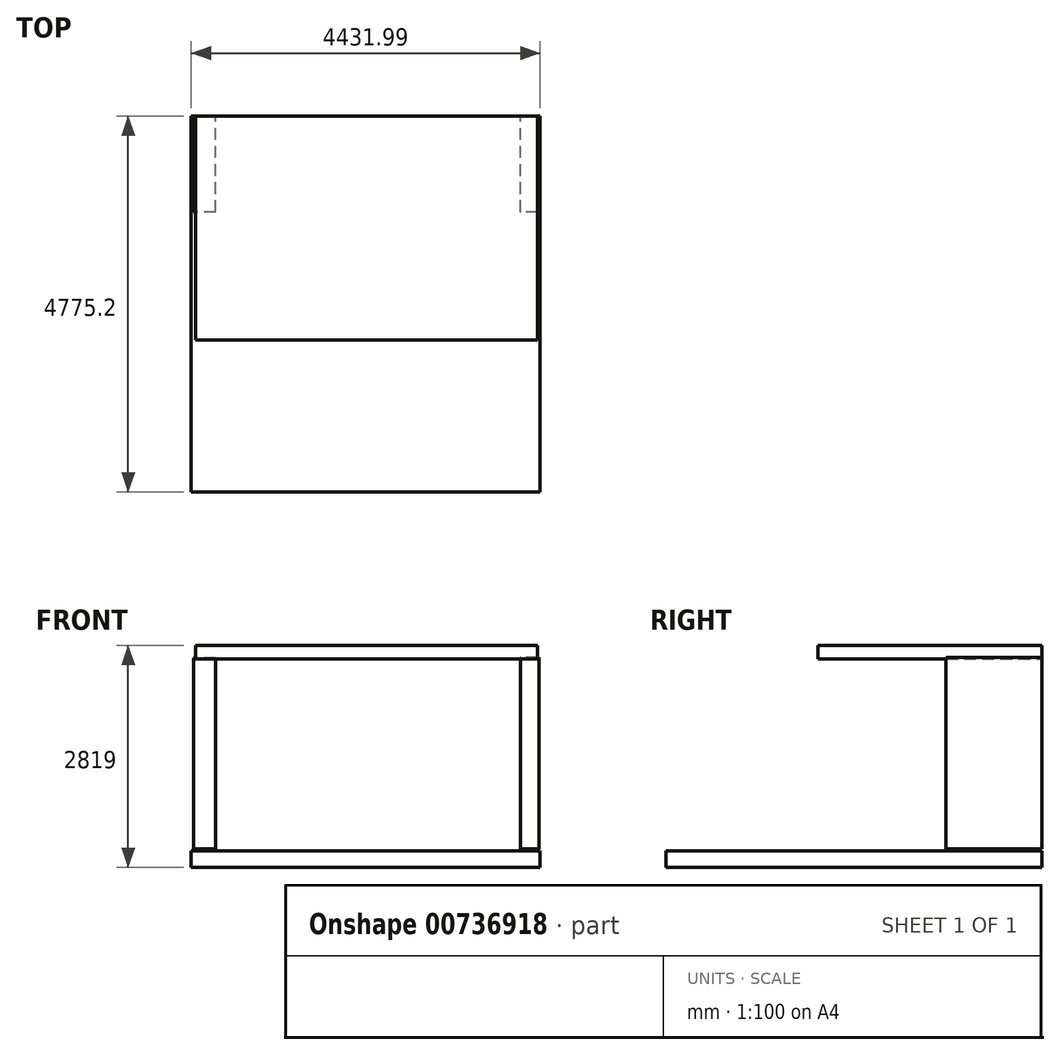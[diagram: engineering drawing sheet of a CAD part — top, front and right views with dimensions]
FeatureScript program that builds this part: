
annotation { "Feature Type Name" : "Feature", "Feature Type Description" : "" }
export const myFeature = defineFeature(function(context is Context, id is Id, definition is map)
    precondition{}
    {
        {
            var Q0;
            Q0=qCreatedBy(makeId("Front.planeOp"),FACE);
            var sketch = newSketch(context, id + "F0", { "sketchPlane" : qUnion([Q0])});
            skLineSegment(sketch, "E0.bottom", {"start": v(-1929.35, 1211.68) * mm, "end": v(-2210.09, 1211.68) * mm});
            skLineSegment(sketch, "E0.top", {"start": v(-1929.35, -1217.43) * mm, "end": v(-2210.09, -1217.43) * mm});
            skLineSegment(sketch, "E0.left", {"start": v(-1929.35, 1211.68) * mm, "end": v(-1929.35, -1217.43) * mm});
            skLineSegment(sketch, "E0.right", {"start": v(-2210.09, 1211.68) * mm, "end": v(-2210.09, -1217.43) * mm});
            skLineSegment(sketch, "E1.bottom", {"start": v(2176.34, 1214.56) * mm, "end": v(1940.93, 1214.56) * mm});
            skLineSegment(sketch, "E1.top", {"start": v(2176.34, -1214.56) * mm, "end": v(1940.93, -1214.56) * mm});
            skLineSegment(sketch, "E1.left", {"start": v(2176.34, 1214.56) * mm, "end": v(2176.34, -1214.56) * mm});
            skLineSegment(sketch, "E1.right", {"start": v(1940.93, 1214.56) * mm, "end": v(1940.93, -1214.56) * mm});
            skSolve(sketch);
        }
        {
            var Q0;
            Q0=makeQuery(id+"F0.imprint","IMPRINT",FACE,{"disambiguationData":[TD([[makeQuery(id+"F0.imprint","IMPRINT",EDGE,{"derivedFrom":sQuery(id+"F0.wireOp",EDGE,"E0.bottom")}),1.0]])]});
            var Q1;
            Q1=makeQuery(id+"F0.imprint","IMPRINT",FACE,{"disambiguationData":[TD([[makeQuery(id+"F0.imprint","IMPRINT",EDGE,{"derivedFrom":sQuery(id+"F0.wireOp",EDGE,"E1.bottom")}),1.0]])]});
            extrude(context, id + "F1", {"entities" : qUnion([Q0, Q1]), "depth" : 1219.2 * mm, "offsetDistance" : 25.4 * mm});
        }
        {
            var Q0;
            Q0=qCreatedBy(makeId("Front.planeOp"),FACE);
            var sketch = newSketch(context, id + "F2", { "sketchPlane" : qUnion([Q0])});
            skLineSegment(sketch, "E2.bottom", {"start": v(2160.31, 1199.62) * mm, "end": v(-2187.19, 1199.62) * mm});
            skLineSegment(sketch, "E2.top", {"start": v(2160.31, 1369.04) * mm, "end": v(-2187.19, 1369.04) * mm});
            skLineSegment(sketch, "E2.left", {"start": v(2160.31, 1199.62) * mm, "end": v(2160.31, 1369.04) * mm});
            skLineSegment(sketch, "E2.right", {"start": v(-2187.19, 1199.62) * mm, "end": v(-2187.19, 1369.04) * mm});
            skSolve(sketch);
        }
        {
            var Q0;
            Q0 = qSketchRegion(id + "F2", true);
            extrude(context, id + "F3", {"entities" : qUnion([Q0]), "depth" : 2844.8 * mm, "offsetDistance" : 25.4 * mm});
        }
        {
            var Q0;
            Q0=qCreatedBy(makeId("Front.planeOp"),FACE);
            var sketch = newSketch(context, id + "F4", { "sketchPlane" : qUnion([Q0])});
            skLineSegment(sketch, "E3.bottom", {"start": v(-2239.35, -1239.9) * mm, "end": v(2192.64, -1239.9) * mm});
            skLineSegment(sketch, "E3.top", {"start": v(-2239.35, -1449.96) * mm, "end": v(2192.64, -1449.96) * mm});
            skLineSegment(sketch, "E3.left", {"start": v(-2239.35, -1239.9) * mm, "end": v(-2239.35, -1449.96) * mm});
            skLineSegment(sketch, "E3.right", {"start": v(2192.64, -1239.9) * mm, "end": v(2192.64, -1449.96) * mm});
            skSolve(sketch);
        }
        {
            var Q0;
            Q0 = qSketchRegion(id + "F4", true);
            extrude(context, id + "F5", {"entities" : qUnion([Q0]), "depth" : 4775.2 * mm, "offsetDistance" : 25.4 * mm});
        }
    });
